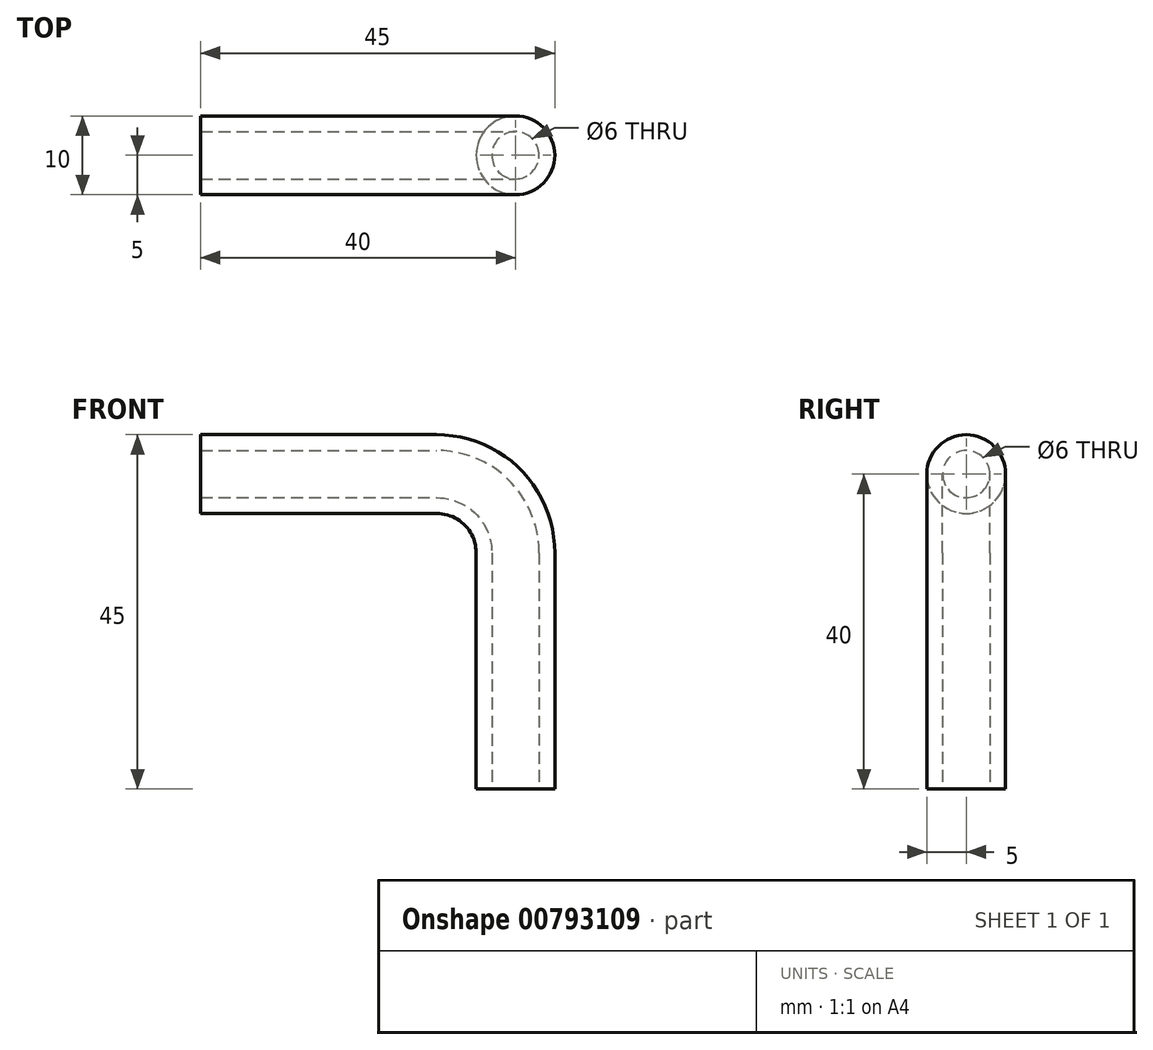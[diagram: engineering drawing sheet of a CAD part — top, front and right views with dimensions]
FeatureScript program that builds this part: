
annotation { "Feature Type Name" : "Feature", "Feature Type Description" : "" }
export const myFeature = defineFeature(function(context is Context, id is Id, definition is map)
    precondition{}
    {
        {
            var Q0;
            Q0=qCreatedBy(makeId("Right.planeOp"),FACE);
            var sketch = newSketch(context, id + "F0", { "sketchPlane" : qUnion([Q0])});
            skCircle(sketch, "E0", {"center": v(0, 0) * mm, "radius": 3 * mm});
            skCircle(sketch, "E1", {"center": v(0, 0) * mm, "radius": 5 * mm});
            skSolve(sketch);
        }
        {
            var Q0;
            Q0=makeQuery(id+"F0.imprint","IMPRINT",FACE,{"disambiguationData":[TD([[makeQuery(id+"F0.imprint","IMPRINT",EDGE,{"derivedFrom":sQuery(id+"F0.wireOp",EDGE,"E0")}),-1.0]])]});
            extrude(context, id + "F1", {"entities" : qUnion([Q0]), "oppositeDirection" : true, "depth" : 30 * mm, "offsetDistance" : 25 * mm, "flatOperationType" : FlatOperationType.REMOVE, "domain" : OperationDomain.MODEL});
        }
        {
            var Q0;
            Q0=qCreatedBy(makeId("Front.planeOp"),FACE);
            var sketch = newSketch(context, id + "F2", { "sketchPlane" : qUnion([Q0])});
            skPoint(sketch, "E2", {"position": v(0, -10) * mm});
            skArc(sketch, "E3", {"start": v(0, 0) * mm, "mid": v(7.07, -2.93) * mm, "end": v(10, -10) * mm});
            skLineSegment(sketch, "E4", {"start": v(10, -10) * mm, "end": v(10, -40) * mm});
            skSolve(sketch);
        }
        {
            var Q0;
            Q0=makeQuery(id+"F1.opExtrude","CAP_FACE",FACE,{"disambiguationData":[OSD([sQuery(id+"F0.wireOp",EDGE,"E0"),sQuery(id+"F0.wireOp",EDGE,"E1")])],"isStart":true});
            var Q1;
            Q1=sQuery(id+"F2.wireOp",EDGE,"E3");
            var Q2;
            Q2=sQuery(id+"F2.wireOp",EDGE,"E4");
            sweep(context, id + "F3", {"operationType" : NewBodyOperationType.ADD, "profiles" : qUnion([Q0]), "path" : qUnion([Q1, Q2])});
        }
    });
